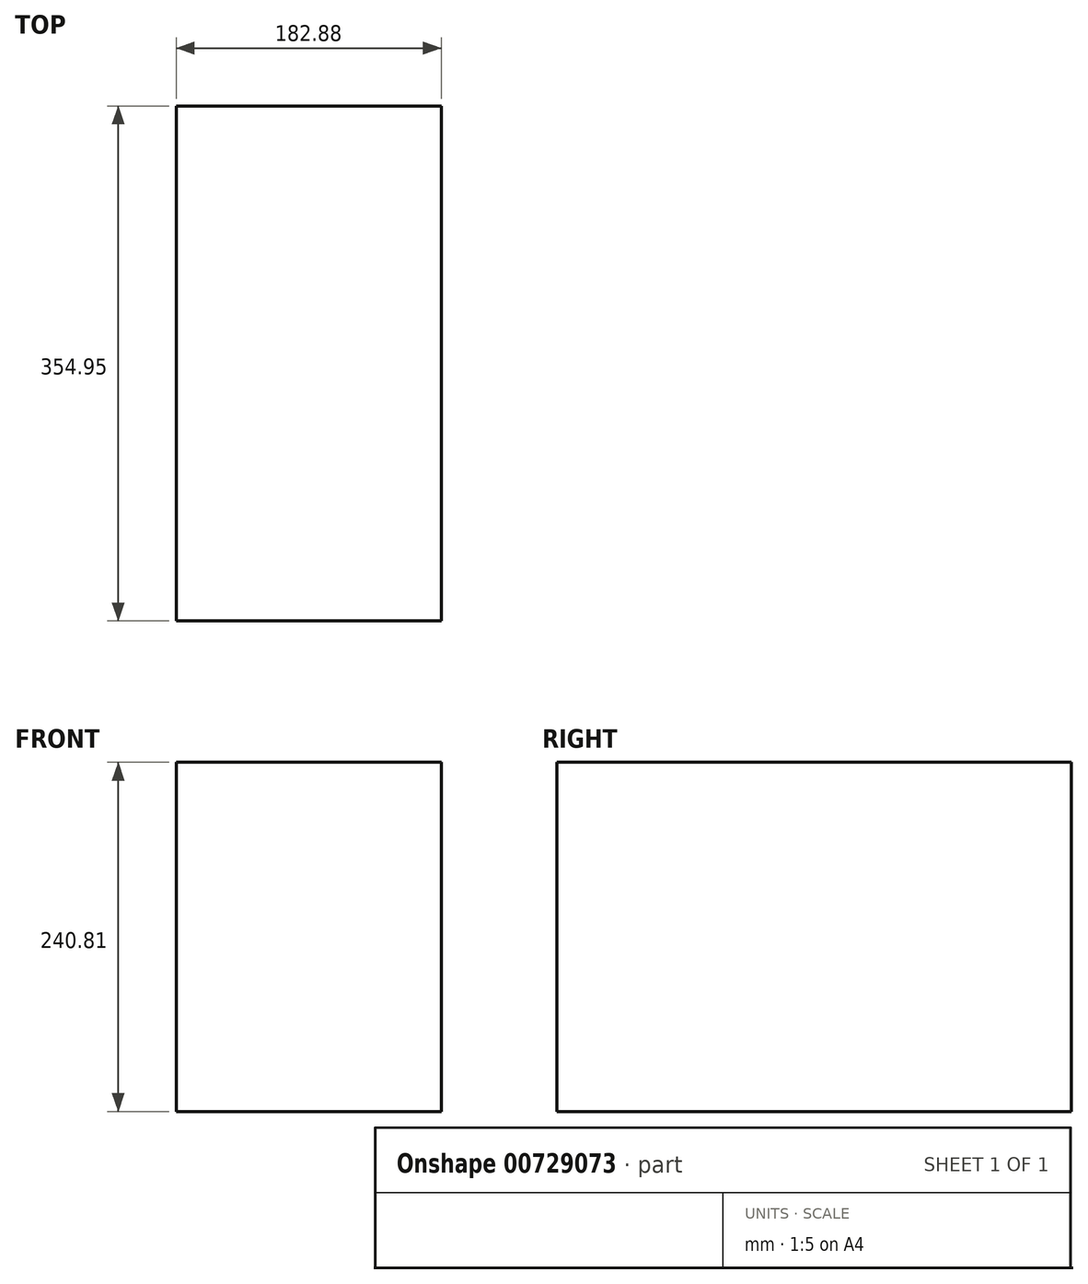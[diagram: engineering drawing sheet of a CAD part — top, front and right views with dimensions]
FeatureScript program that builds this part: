
annotation { "Feature Type Name" : "Feature", "Feature Type Description" : "" }
export const myFeature = defineFeature(function(context is Context, id is Id, definition is map)
    precondition{}
    {
        {
            var Q0;
            Q0=qCreatedBy(makeId("Right.planeOp"),FACE);
            var sketch = newSketch(context, id + "F0", { "sketchPlane" : qUnion([Q0])});
            skLineSegment(sketch, "E0.bottom", {"start": v(-173.37, 134.78) * mm, "end": v(181.58, 134.78) * mm});
            skLineSegment(sketch, "E0.top", {"start": v(-173.37, -106.03) * mm, "end": v(181.58, -106.03) * mm});
            skLineSegment(sketch, "E0.left", {"start": v(-173.37, 134.78) * mm, "end": v(-173.37, -106.03) * mm});
            skLineSegment(sketch, "E0.right", {"start": v(181.58, 134.78) * mm, "end": v(181.58, -106.03) * mm});
            skSolve(sketch);
        }
        {
            var Q0;
            Q0=makeQuery(id+"F0.imprint","IMPRINT",FACE,{"disambiguationData":[TD([[makeQuery(id+"F0.imprint","IMPRINT",EDGE,{"derivedFrom":sQuery(id+"F0.wireOp",EDGE,"E0.bottom")}),-1.0]])]});
            extrude(context, id + "F1", {"entities" : qUnion([Q0]), "depth" : 182.88 * mm, "offsetDistance" : 25.4 * mm});
        }
    });
